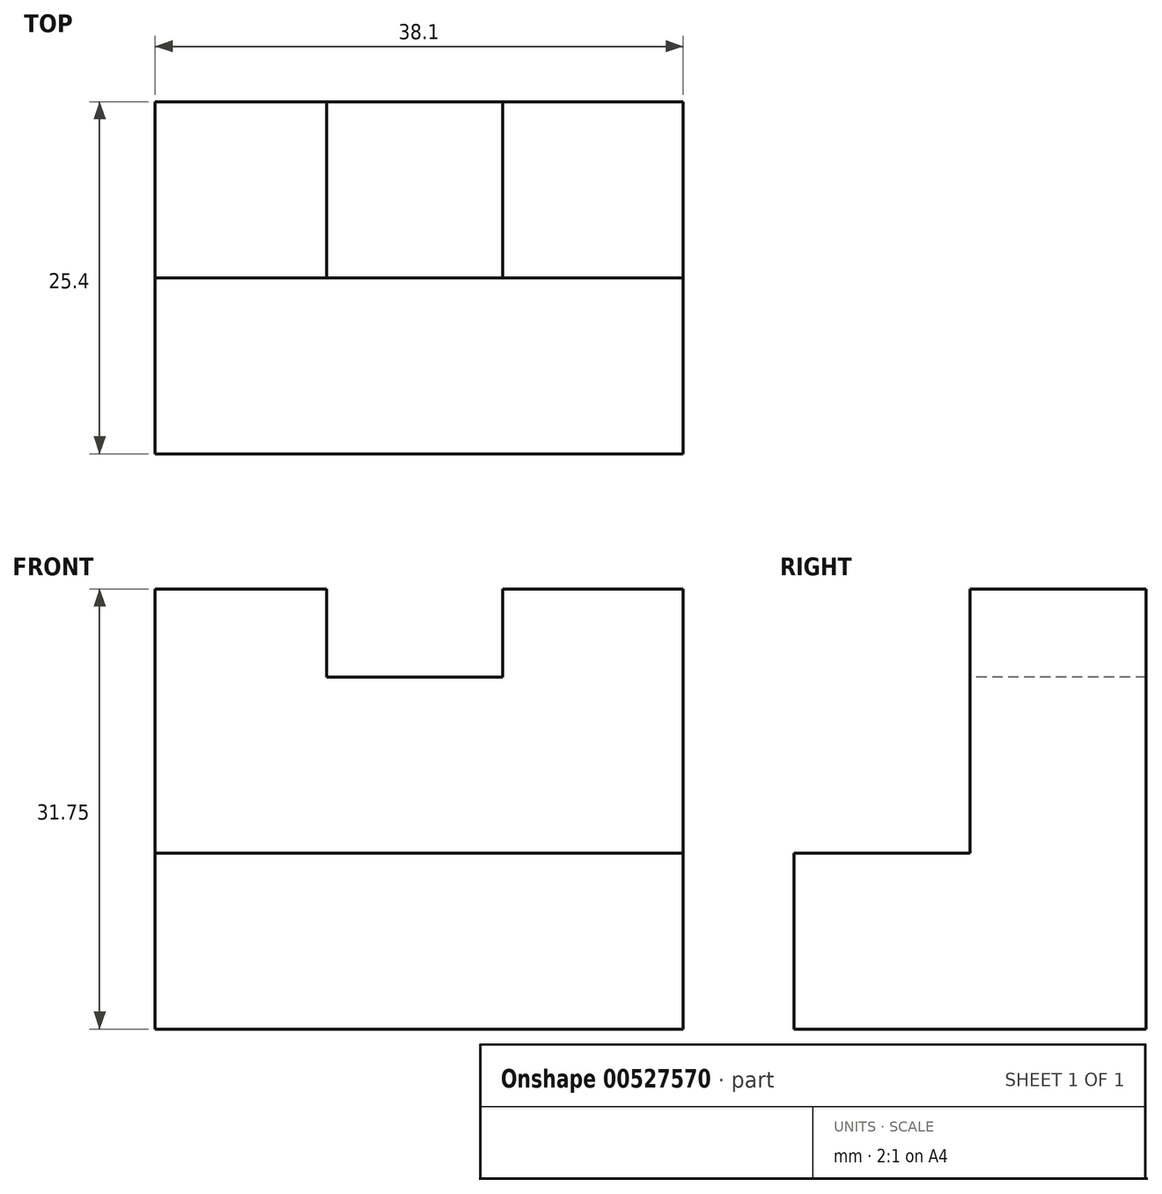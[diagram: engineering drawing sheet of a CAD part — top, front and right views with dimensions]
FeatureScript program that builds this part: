
annotation { "Feature Type Name" : "Feature", "Feature Type Description" : "" }
export const myFeature = defineFeature(function(context is Context, id is Id, definition is map)
    precondition{}
    {
        {
            var Q0;
            Q0=qCreatedBy(makeId("Right.planeOp"),FACE);
            var sketch = newSketch(context, id + "F0", { "sketchPlane" : qUnion([Q0])});
            skLineSegment(sketch, "E0", {"start": v(0, 0) * mm, "end": v(25.4, 0) * mm});
            skLineSegment(sketch, "E1", {"start": v(25.4, 0) * mm, "end": v(25.4, 31.75) * mm});
            skLineSegment(sketch, "E2", {"start": v(25.4, 31.75) * mm, "end": v(12.7, 31.75) * mm});
            skLineSegment(sketch, "E3", {"start": v(12.7, 31.75) * mm, "end": v(12.7, 12.7) * mm});
            skLineSegment(sketch, "E4", {"start": v(12.7, 12.7) * mm, "end": v(0, 12.7) * mm});
            skLineSegment(sketch, "E5", {"start": v(0, 12.7) * mm, "end": v(0, 0) * mm});
            skSolve(sketch);
        }
        {
            var Q0;
            Q0=makeQuery(id+"F0.imprint","IMPRINT",FACE,{"disambiguationData":[TD([[makeQuery(id+"F0.imprint","IMPRINT",EDGE,{"derivedFrom":sQuery(id+"F0.wireOp",EDGE,"E0")}),1.0]])]});
            extrude(context, id + "F1", {"entities" : qUnion([Q0]), "depth" : 38.1 * mm, "offsetDistance" : 25.4 * mm});
        }
        {
            var Q0;
            Q0=makeQuery(id+"F1.opExtrude","SWEPT_FACE",FACE,{"disambiguationData":[OSD([sQuery(id+"F0.wireOp",EDGE,"E2")])]});
            var sketch = newSketch(context, id + "F2", { "sketchPlane" : qUnion([Q0])});
            skLineSegment(sketch, "E6", {"start": v(12.38, 25.4) * mm, "end": v(12.38, 12.7) * mm});
            skLineSegment(sketch, "E7", {"start": v(25.07, 25.4) * mm, "end": v(25.07, 12.7) * mm});
            skSolve(sketch);
        }
        {
            var Q0;
            {var subQ0=sQuery(id+"F2.wireOp",EDGE,"E6");Q0=makeQuery(id+"F2.imprint","IMPRINT",FACE,{"disambiguationData":[TD([[makeQuery(id+"F2.imprint","IMPRINT",EDGE,{"derivedFrom":subQ0}),1.0]])]});}
            extrude(context, id + "F3", {"entities" : qUnion([Q0]), "operationType" : NewBodyOperationType.REMOVE, "oppositeDirection" : true, "depth" : 6.35 * mm, "offsetDistance" : 25.4 * mm});
        }
    });
